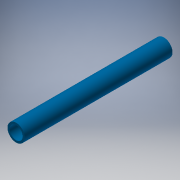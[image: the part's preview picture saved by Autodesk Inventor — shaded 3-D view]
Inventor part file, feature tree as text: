
AUTODESK INVENTOR PART (.ipt)
format: ipt  version: 2018.2 (Build 222227000, 227)  size: 108,032 bytes
history: native  units: in
note: dims shown in document units (in); Inventor stores cm internally (conversion verified against a paired STEP export)
features: extrude x1, sketch x1
ambient origin geometry x8: Origin, YZ Plane, XZ Plane, XY Plane, X Axis, Y Axis, Z Axis, Center Point
bodies: Solid1 (feature_tree)
feature tree (2):
  extrude  "Extrusion1"  Depth=11.25in
  sketch  "Sketch1"  dims[d0=1.315in d1=1.0in d2=11.25in d3=0.0in]
